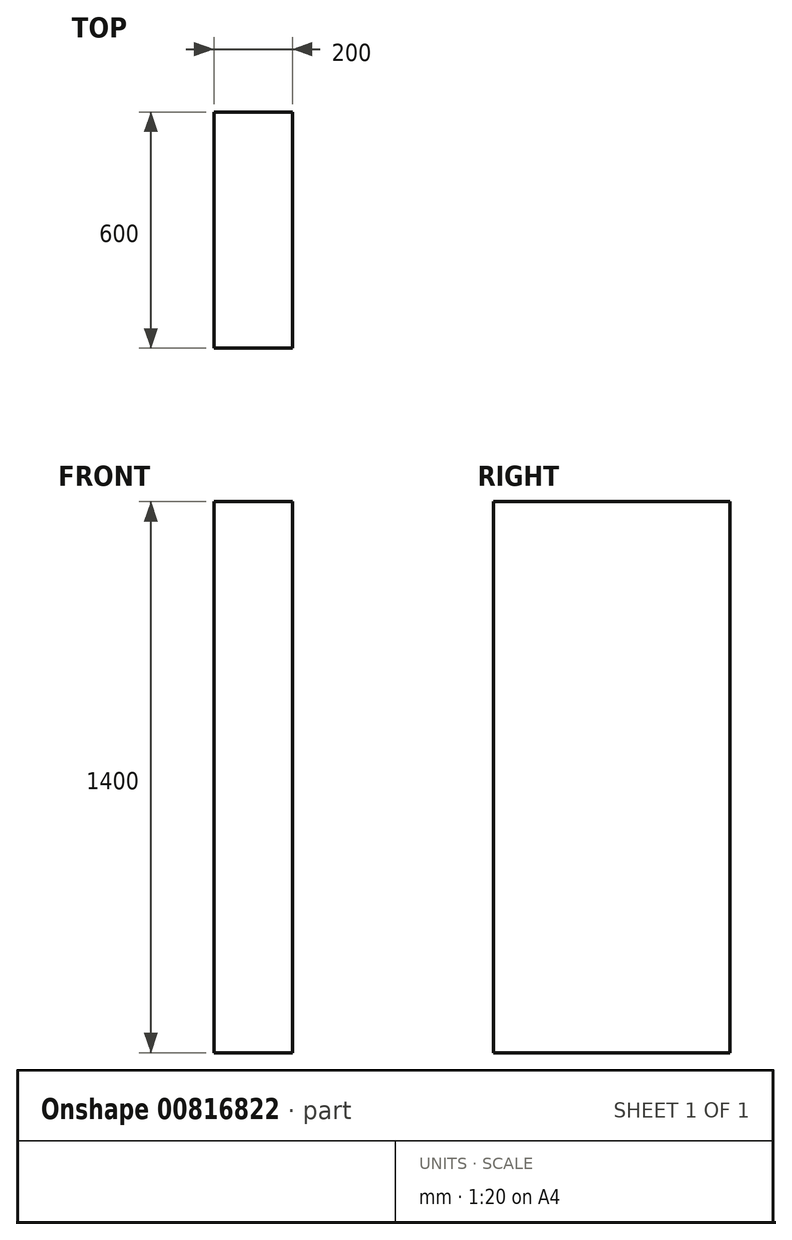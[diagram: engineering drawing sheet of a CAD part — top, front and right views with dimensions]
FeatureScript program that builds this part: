
annotation { "Feature Type Name" : "Feature", "Feature Type Description" : "" }
export const myFeature = defineFeature(function(context is Context, id is Id, definition is map)
    precondition{}
    {
        {
            var Q0;
            Q0=qCreatedBy(makeId("Front.planeOp"),FACE);
            var sketch = newSketch(context, id + "F0", { "sketchPlane" : qUnion([Q0])});
            skLineSegment(sketch, "E0.bottom", {"start": v(0, 0) * mm, "end": v(-200, 0) * mm});
            skLineSegment(sketch, "E0.top", {"start": v(0, 1400) * mm, "end": v(-200, 1400) * mm});
            skLineSegment(sketch, "E0.left", {"start": v(0, 0) * mm, "end": v(0, 1400) * mm});
            skLineSegment(sketch, "E0.right", {"start": v(-200, 0) * mm, "end": v(-200, 1400) * mm});
            skSolve(sketch);
        }
        {
            var Q0;
            Q0=makeQuery(id+"F0.imprint","IMPRINT",FACE,{"disambiguationData":[TD([[makeQuery(id+"F0.imprint","IMPRINT",EDGE,{"derivedFrom":sQuery(id+"F0.wireOp",EDGE,"E0.bottom")}),-1.0]])]});
            extrude(context, id + "F1", {"entities" : qUnion([Q0]), "depth" : 600 * mm, "offsetDistance" : 25 * mm});
        }
    });
